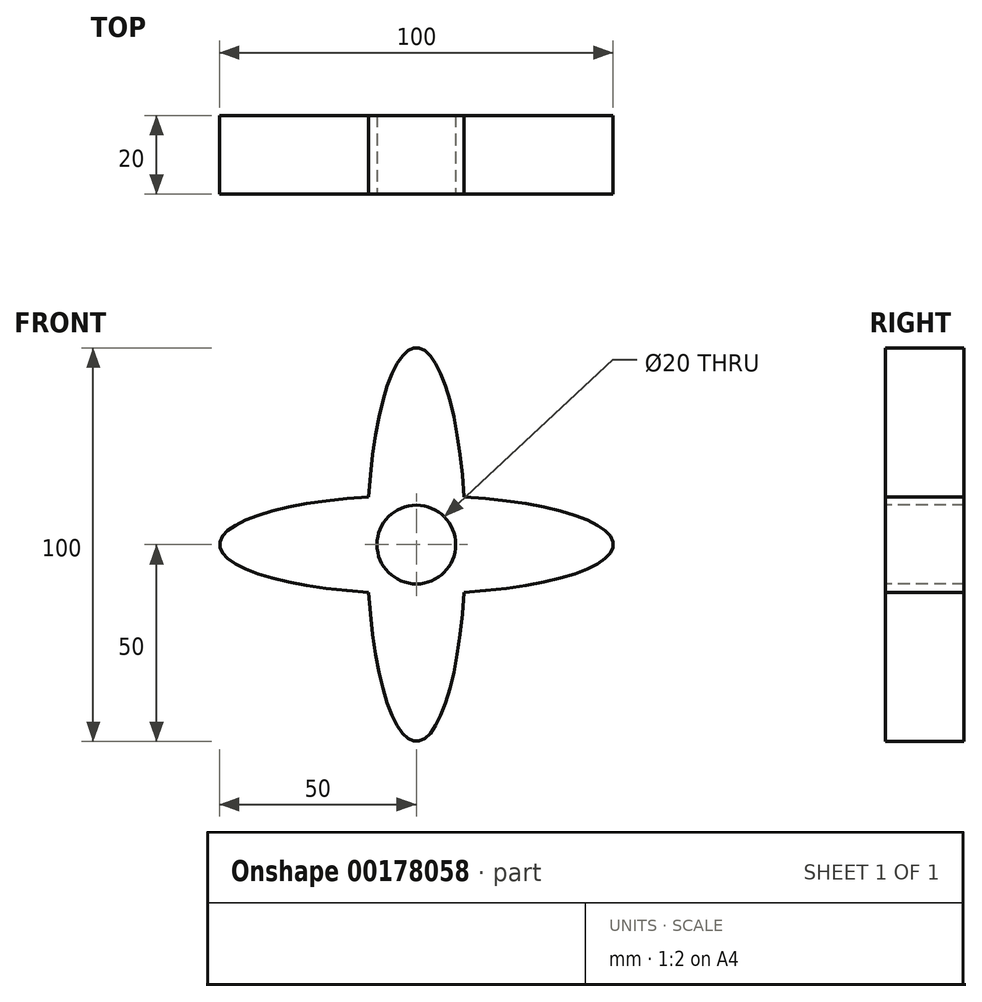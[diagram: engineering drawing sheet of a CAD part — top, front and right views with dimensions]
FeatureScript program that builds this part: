
annotation { "Feature Type Name" : "Feature", "Feature Type Description" : "" }
export const myFeature = defineFeature(function(context is Context, id is Id, definition is map)
    precondition{}
    {
        {
            var Q0;
            Q0=qCreatedBy(makeId("Front.planeOp"),FACE);
            var sketch = newSketch(context, id + "F0", { "sketchPlane" : qUnion([Q0])});
            skEllipse(sketch, "E0", {"center": v(0, 0) * mm, "majorRadius": 50 * mm, "minorRadius": 12.5 * mm, "majorAxis": v(0, 1)});
            skEllipse(sketch, "E1", {"center": v(0, 0) * mm, "majorRadius": 50 * mm, "minorRadius": 12.5 * mm, "majorAxis": v(1, 0)});
            skSolve(sketch);
        }
        {
            var Q0;
            Q0 = qSketchRegion(id + "F0", true);
            extrude(context, id + "F1", {"entities" : qUnion([Q0]), "depth" : 20 * mm});
        }
        {
            var Q0;
            Q0=makeQuery(id+"F1.opExtrude","CAP_FACE",FACE,{"disambiguationData":[OSD([sQuery(id+"F0.wireOp",EDGE,"E0"),sQuery(id+"F0.wireOp",EDGE,"E1")])],"isStart":false});
            var sketch = newSketch(context, id + "F2", { "sketchPlane" : qUnion([Q0])});
            skCircle(sketch, "E2", {"center": v(0, 0) * mm, "radius": 10 * mm});
            skSolve(sketch);
        }
        {
            var Q0;
            Q0 = qSketchRegion(id + "F2", true);
            extrude(context, id + "F3", {"entities" : qUnion([Q0]), "operationType" : NewBodyOperationType.REMOVE, "endBound" : BoundingType.THROUGH_ALL, "oppositeDirection" : true, "depth" : 25 * mm});
        }
    });
